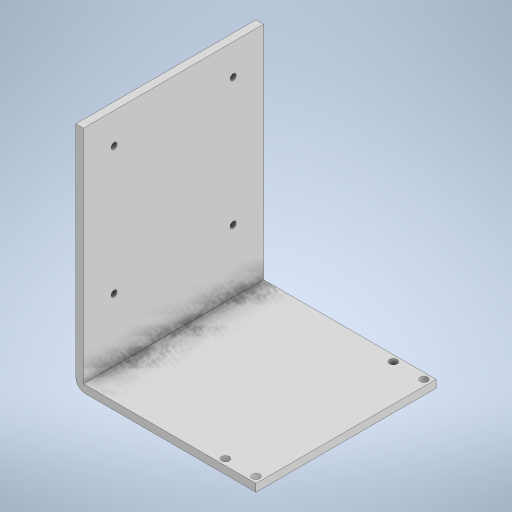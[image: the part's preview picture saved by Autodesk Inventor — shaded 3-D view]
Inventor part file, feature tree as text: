
AUTODESK INVENTOR PART (.ipt)
format: ipt  version: 2023 (Build 270158030, 158C)  size: 271,872 bytes
history: native  units: in
note: dims shown in document units (in); Inventor stores cm internally (conversion verified against a paired STEP export)
features: sketch x4, extrude x3, fillet x1, hole x1
ambient origin geometry x8: Origin, YZ Plane, XZ Plane, XY Plane, X Axis, Y Axis, Z Axis, Center Point
bodies: Solid1 (feature_tree)
feature tree (9):
  extrude  "Extrusion1"  Depth=5.5in
  extrude  "Extrusion3"  Depth=1.0in
  extrude  "Extrusion4"  Depth=5.5in
  fillet  "Fillet1"  Radius=0.25in
  hole  "Hole1"  [1 undecoded]
  sketch  "Sketch1"  dims[d0=0.25in d1=5.5in]
  sketch  "Sketch3"  dims[d2=0.25in d3=1.0in]
  sketch  "Sketch4"  dims[d4=0.25in d5=5.5in d6=0.25in]
  sketch  "Sketch5"  dims[d7=0.2in d8=0.2in d9=0.2in d10=0.2in d11=0.25in d12=0.0in d17=4.5in d18=0.0in d19=0.25in d20=7.25in d21=0.0in d22=0.3125in d23=1.0in d24=1.0in d25=1.0in d26=1.0in d27=1.0in d29=2.0in d30=1.0in d31=2.0in d32=90.0deg d33=0.196in d34=0.5in d35=0.375in d36=0.25in d37=0.5635in d38=0.75in d39=0.8108in]
note: 1 required parameter value undecoded (feature->parameter linkage not recoverable at this tier; creation-order binding heuristic only, values carry confidence <= 0.55)
